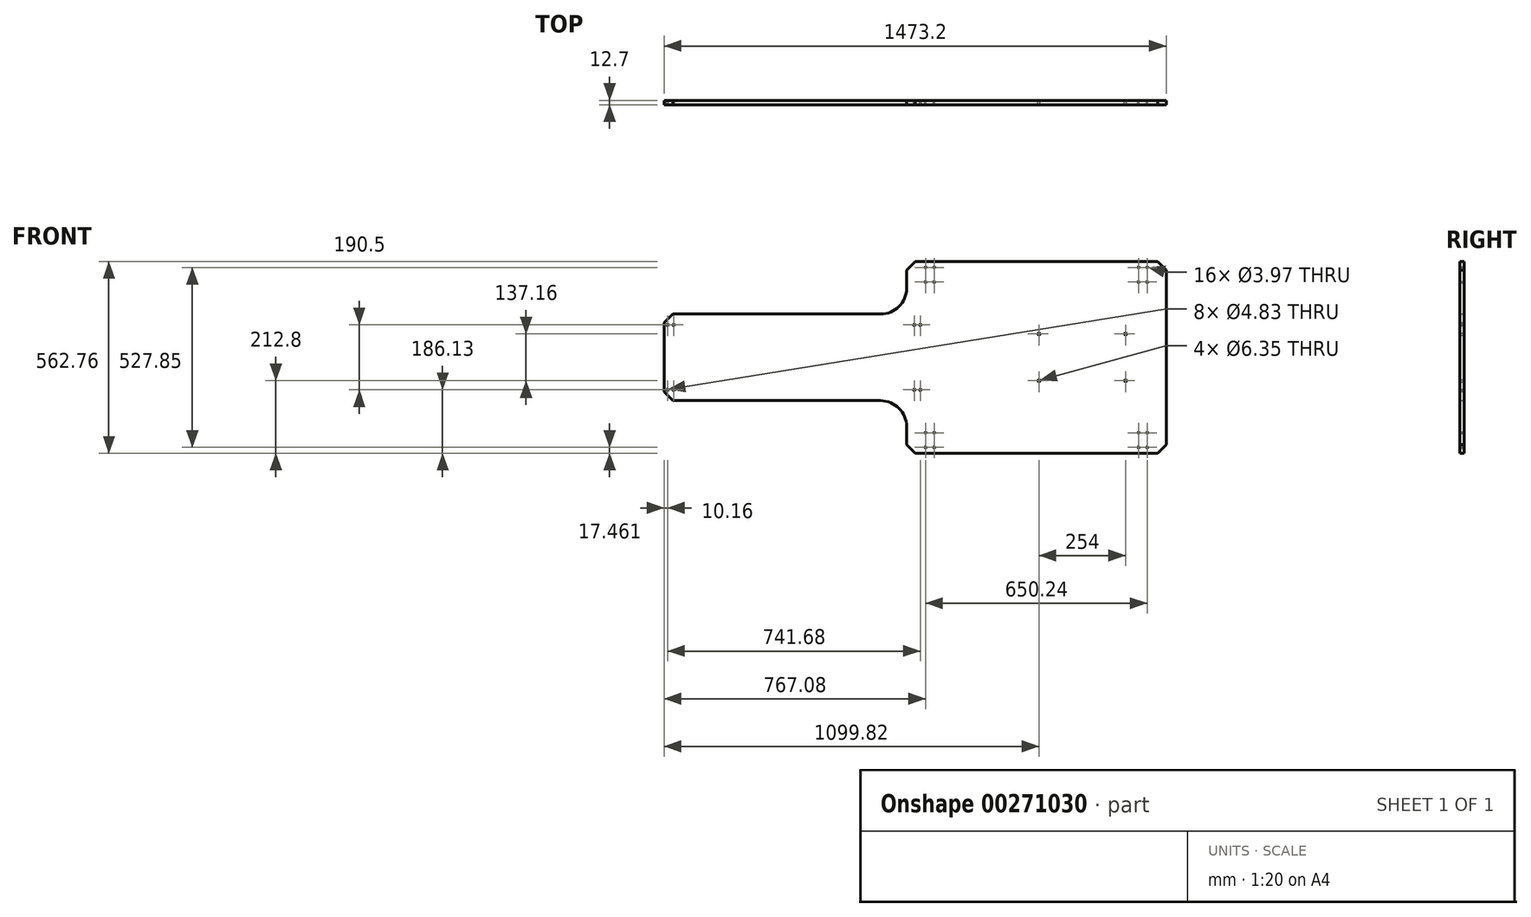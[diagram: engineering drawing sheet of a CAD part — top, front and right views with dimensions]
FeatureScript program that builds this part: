
annotation { "Feature Type Name" : "Feature", "Feature Type Description" : "" }
export const myFeature = defineFeature(function(context is Context, id is Id, definition is map)
    precondition{}
    {
        {
            var Q0;
            Q0=qCreatedBy(makeId("Front.planeOp"),FACE);
            var sketch = newSketch(context, id + "F0", { "sketchPlane" : qUnion([Q0])});
            skLineSegment(sketch, "E0.bottom", {"start": v(0, 0) * mm, "end": v(635, 0) * mm});
            skLineSegment(sketch, "E0.top", {"start": v(0, 254) * mm, "end": v(635, 254) * mm});
            skLineSegment(sketch, "E0.left", {"start": v(0, 0) * mm, "end": v(0, 254) * mm});
            skLineSegment(sketch, "E1.bottom", {"start": v(711.2, -154.38) * mm, "end": v(1473.2, -154.38) * mm});
            skLineSegment(sketch, "E1.top", {"start": v(711.2, 408.38) * mm, "end": v(1473.2, 408.38) * mm});
            skLineSegment(sketch, "E1.left", {"start": v(711.2, -154.38) * mm, "end": v(711.2, -76.2) * mm});
            skLineSegment(sketch, "E1.right", {"start": v(1473.2, -154.38) * mm, "end": v(1473.2, 408.38) * mm});
            skLineSegment(sketch, "E2.trimOffspring", {"start": v(711.2, 330.2) * mm, "end": v(711.2, 408.38) * mm});
            skPoint(sketch, "E3.visualSharp", {"position": v(711.2, 254) * mm});
            skArc(sketch, "E3.filletArc", {"start": v(635, 254) * mm, "mid": v(688.88, 276.32) * mm, "end": v(711.2, 330.2) * mm});
            skPoint(sketch, "E4.visualSharp", {"position": v(711.2, 0) * mm});
            skArc(sketch, "E4.filletArc", {"start": v(711.2, -76.2) * mm, "mid": v(688.88, -22.32) * mm, "end": v(635, 0) * mm});
            skSolve(sketch);
        }
        {
            var Q0;
            Q0 = qSketchRegion(id + "F0", true);
            extrude(context, id + "F1", {"entities" : qUnion([Q0]), "depth" : 12.7 * mm});
        }
        {
            var Q0;
            Q0=makeQuery(id+"F1.opExtrude","SWEPT_EDGE",EDGE,{"disambiguationData":[OSD([sQuery(id+"F0.wireOp",EDGE,"E1.top"),sQuery(id+"F0.wireOp",EDGE,"E2.trimOffspring")])]});
            var Q1;
            Q1=makeQuery(id+"F1.opExtrude","SWEPT_EDGE",EDGE,{"disambiguationData":[OSD([sQuery(id+"F0.wireOp",EDGE,"E1.top"),sQuery(id+"F0.wireOp",EDGE,"E1.right")])]});
            var Q2;
            Q2=makeQuery(id+"F1.opExtrude","SWEPT_EDGE",EDGE,{"disambiguationData":[OSD([sQuery(id+"F0.wireOp",EDGE,"E1.bottom"),sQuery(id+"F0.wireOp",EDGE,"E1.right")])]});
            var Q3;
            Q3=makeQuery(id+"F1.opExtrude","SWEPT_EDGE",EDGE,{"disambiguationData":[OSD([sQuery(id+"F0.wireOp",EDGE,"E1.bottom"),sQuery(id+"F0.wireOp",EDGE,"E1.left")])]});
            var Q4;
            Q4=makeQuery(id+"F1.opExtrude","SWEPT_EDGE",EDGE,{"disambiguationData":[OSD([sQuery(id+"F0.wireOp",EDGE,"E0.bottom"),sQuery(id+"F0.wireOp",EDGE,"E0.left")])]});
            var Q5;
            Q5=makeQuery(id+"F1.opExtrude","SWEPT_EDGE",EDGE,{"disambiguationData":[OSD([sQuery(id+"F0.wireOp",EDGE,"E0.top"),sQuery(id+"F0.wireOp",EDGE,"E0.left")])]});
            chamfer(context, id + "F2", {"entities" : qUnion([Q0, Q1, Q2, Q3, Q4, Q5]), "width" : 25.4 * mm, "tangentPropagation" : true});
        }
        {
            var Q0;
            Q0=makeQuery(id+"F1.opExtrude","CAP_FACE",FACE,{"disambiguationData":[OSD([sQuery(id+"F0.wireOp",EDGE,"E0.bottom"),sQuery(id+"F0.wireOp",EDGE,"E0.top"),sQuery(id+"F0.wireOp",EDGE,"E0.left"),sQuery(id+"F0.wireOp",EDGE,"E1.bottom"),sQuery(id+"F0.wireOp",EDGE,"E1.top"),sQuery(id+"F0.wireOp",EDGE,"E1.left"),sQuery(id+"F0.wireOp",EDGE,"E1.right"),sQuery(id+"F0.wireOp",EDGE,"E2.trimOffspring"),sQuery(id+"F0.wireOp",EDGE,"E3.filletArc"),sQuery(id+"F0.wireOp",EDGE,"E4.filletArc")])],"isStart":false});
            var sketch = newSketch(context, id + "F3", { "sketchPlane" : qUnion([Q0])});
            skPoint(sketch, "E5", {"position": v(1391.92, -94.06) * mm});
            skPoint(sketch, "E6", {"position": v(1417.32, -94.06) * mm});
            skPoint(sketch, "E7", {"position": v(1391.92, -136.92) * mm});
            skPoint(sketch, "E8", {"position": v(1417.32, -136.92) * mm});
            skPoint(sketch, "E9", {"position": v(767.08, -94.06) * mm});
            skPoint(sketch, "E10", {"position": v(792.48, -94.06) * mm});
            skPoint(sketch, "E11", {"position": v(792.48, -136.92) * mm});
            skPoint(sketch, "E12", {"position": v(767.08, -136.92) * mm});
            skPoint(sketch, "E13", {"position": v(767.08, 390.93) * mm});
            skPoint(sketch, "E14", {"position": v(792.48, 390.93) * mm});
            skPoint(sketch, "E15", {"position": v(792.48, 348.06) * mm});
            skPoint(sketch, "E16", {"position": v(767.08, 348.06) * mm});
            skPoint(sketch, "E17", {"position": v(1391.92, 348.06) * mm});
            skPoint(sketch, "E18", {"position": v(1391.92, 390.93) * mm});
            skPoint(sketch, "E19", {"position": v(1417.32, 390.93) * mm});
            skPoint(sketch, "E20", {"position": v(1417.32, 348.06) * mm});
            skSolve(sketch);
        }
        {
            var Q0;
            Q0=sQuery(id+"F3.wireOp",VERTEX,"E13");
            var Q1;
            Q1=sQuery(id+"F3.wireOp",VERTEX,"E16");
            var Q2;
            Q2=sQuery(id+"F3.wireOp",VERTEX,"E15");
            var Q3;
            Q3=sQuery(id+"F3.wireOp",VERTEX,"E14");
            var Q4;
            Q4=sQuery(id+"F3.wireOp",VERTEX,"E9");
            var Q5;
            Q5=sQuery(id+"F3.wireOp",VERTEX,"E12");
            var Q6;
            Q6=sQuery(id+"F3.wireOp",VERTEX,"E11");
            var Q7;
            Q7=sQuery(id+"F3.wireOp",VERTEX,"E10");
            var Q8;
            Q8=sQuery(id+"F3.wireOp",VERTEX,"E5");
            var Q9;
            Q9=sQuery(id+"F3.wireOp",VERTEX,"E7");
            var Q10;
            Q10=sQuery(id+"F3.wireOp",VERTEX,"E8");
            var Q11;
            Q11=sQuery(id+"F3.wireOp",VERTEX,"E6");
            var Q12;
            Q12=sQuery(id+"F3.wireOp",VERTEX,"E17");
            var Q13;
            Q13=sQuery(id+"F3.wireOp",VERTEX,"E18");
            var Q14;
            Q14=sQuery(id+"F3.wireOp",VERTEX,"E19");
            var Q15;
            Q15=sQuery(id+"F3.wireOp",VERTEX,"E20");
            var Q16;
            Q16=makeQuery(id+"F1.opExtrude","SWEPT_BODY",BODY,{"disambiguationData":[OSD([sQuery(id+"F0.wireOp",EDGE,"E0.bottom"),sQuery(id+"F0.wireOp",EDGE,"E0.top"),sQuery(id+"F0.wireOp",EDGE,"E0.left"),sQuery(id+"F0.wireOp",EDGE,"E1.bottom"),sQuery(id+"F0.wireOp",EDGE,"E1.top"),sQuery(id+"F0.wireOp",EDGE,"E1.left"),sQuery(id+"F0.wireOp",EDGE,"E1.right"),sQuery(id+"F0.wireOp",EDGE,"E2.trimOffspring"),sQuery(id+"F0.wireOp",EDGE,"E3.filletArc"),sQuery(id+"F0.wireOp",EDGE,"E4.filletArc")])]});
            hole(context, id + "F4", {"style" : HoleStyle.SIMPLE, "endStyle" : HoleEndStyle.THROUGH, "holeDiameter" : 3.97 * mm, "tappedDepth" : 12.7 * mm, "tapClearance" : 3, "locations" : qUnion([Q0, Q1, Q2, Q3, Q4, Q5, Q6, Q7, Q8, Q9, Q10, Q11, Q12, Q13, Q14, Q15]), "scope" : qUnion([Q16])});
        }
        {
            var Q0;
            Q0=makeQuery(id+"F1.opExtrude","CAP_FACE",FACE,{"disambiguationData":[OSD([sQuery(id+"F0.wireOp",EDGE,"E0.bottom"),sQuery(id+"F0.wireOp",EDGE,"E0.top"),sQuery(id+"F0.wireOp",EDGE,"E0.left"),sQuery(id+"F0.wireOp",EDGE,"E1.bottom"),sQuery(id+"F0.wireOp",EDGE,"E1.top"),sQuery(id+"F0.wireOp",EDGE,"E1.left"),sQuery(id+"F0.wireOp",EDGE,"E1.right"),sQuery(id+"F0.wireOp",EDGE,"E2.trimOffspring"),sQuery(id+"F0.wireOp",EDGE,"E3.filletArc"),sQuery(id+"F0.wireOp",EDGE,"E4.filletArc")])],"isStart":false});
            var sketch = newSketch(context, id + "F5", { "sketchPlane" : qUnion([Q0])});
            skPoint(sketch, "E21", {"position": v(1099.82, 195.58) * mm});
            skPoint(sketch, "E22", {"position": v(1353.82, 195.58) * mm});
            skPoint(sketch, "E23", {"position": v(1353.82, 58.42) * mm});
            skPoint(sketch, "E24", {"position": v(1099.82, 58.42) * mm});
            skSolve(sketch);
        }
        {
            var Q0;
            Q0=sQuery(id+"F5.wireOp",VERTEX,"E21");
            var Q1;
            Q1=sQuery(id+"F5.wireOp",VERTEX,"E24");
            var Q2;
            Q2=sQuery(id+"F5.wireOp",VERTEX,"E23");
            var Q3;
            Q3=sQuery(id+"F5.wireOp",VERTEX,"E22");
            var Q4;
            Q4=makeQuery(id+"F1.opExtrude","SWEPT_BODY",BODY,{"disambiguationData":[OSD([sQuery(id+"F0.wireOp",EDGE,"E0.bottom"),sQuery(id+"F0.wireOp",EDGE,"E0.top"),sQuery(id+"F0.wireOp",EDGE,"E0.left"),sQuery(id+"F0.wireOp",EDGE,"E1.bottom"),sQuery(id+"F0.wireOp",EDGE,"E1.top"),sQuery(id+"F0.wireOp",EDGE,"E1.left"),sQuery(id+"F0.wireOp",EDGE,"E1.right"),sQuery(id+"F0.wireOp",EDGE,"E2.trimOffspring"),sQuery(id+"F0.wireOp",EDGE,"E3.filletArc"),sQuery(id+"F0.wireOp",EDGE,"E4.filletArc")])]});
            hole(context, id + "F6", {"style" : HoleStyle.SIMPLE, "endStyle" : HoleEndStyle.THROUGH, "holeDiameter" : 6.35 * mm, "tappedDepth" : 12.7 * mm, "tapClearance" : 3, "locations" : qUnion([Q0, Q1, Q2, Q3]), "scope" : qUnion([Q4])});
        }
        {
            var Q0;
            Q0=makeQuery(id+"F1.opExtrude","CAP_FACE",FACE,{"disambiguationData":[OSD([sQuery(id+"F0.wireOp",EDGE,"E0.bottom"),sQuery(id+"F0.wireOp",EDGE,"E0.top"),sQuery(id+"F0.wireOp",EDGE,"E0.left"),sQuery(id+"F0.wireOp",EDGE,"E1.bottom"),sQuery(id+"F0.wireOp",EDGE,"E1.top"),sQuery(id+"F0.wireOp",EDGE,"E1.left"),sQuery(id+"F0.wireOp",EDGE,"E1.right"),sQuery(id+"F0.wireOp",EDGE,"E2.trimOffspring"),sQuery(id+"F0.wireOp",EDGE,"E3.filletArc"),sQuery(id+"F0.wireOp",EDGE,"E4.filletArc")])],"isStart":false});
            var sketch = newSketch(context, id + "F7", { "sketchPlane" : qUnion([Q0])});
            skPoint(sketch, "E25", {"position": v(10.16, 222.25) * mm});
            skPoint(sketch, "E26", {"position": v(27.94, 222.25) * mm});
            skPoint(sketch, "E27", {"position": v(734.06, 222.25) * mm});
            skPoint(sketch, "E28", {"position": v(751.84, 222.25) * mm});
            skPoint(sketch, "E29", {"position": v(10.16, 31.75) * mm});
            skPoint(sketch, "E30", {"position": v(27.94, 31.75) * mm});
            skPoint(sketch, "E31", {"position": v(734.06, 31.75) * mm});
            skPoint(sketch, "E32", {"position": v(751.84, 31.75) * mm});
            skSolve(sketch);
        }
        {
            var Q0;
            Q0=sQuery(id+"F7.wireOp",VERTEX,"E25");
            var Q1;
            Q1=sQuery(id+"F7.wireOp",VERTEX,"E26");
            var Q2;
            Q2=sQuery(id+"F7.wireOp",VERTEX,"E29");
            var Q3;
            Q3=sQuery(id+"F7.wireOp",VERTEX,"E30");
            var Q4;
            Q4=sQuery(id+"F7.wireOp",VERTEX,"E31");
            var Q5;
            Q5=sQuery(id+"F7.wireOp",VERTEX,"E28");
            var Q6;
            Q6=sQuery(id+"F7.wireOp",VERTEX,"E27");
            var Q7;
            Q7=sQuery(id+"F7.wireOp",VERTEX,"E32");
            var Q8;
            Q8=makeQuery(id+"F1.opExtrude","SWEPT_BODY",BODY,{"disambiguationData":[OSD([sQuery(id+"F0.wireOp",EDGE,"E0.bottom"),sQuery(id+"F0.wireOp",EDGE,"E0.top"),sQuery(id+"F0.wireOp",EDGE,"E0.left"),sQuery(id+"F0.wireOp",EDGE,"E1.bottom"),sQuery(id+"F0.wireOp",EDGE,"E1.top"),sQuery(id+"F0.wireOp",EDGE,"E1.left"),sQuery(id+"F0.wireOp",EDGE,"E1.right"),sQuery(id+"F0.wireOp",EDGE,"E2.trimOffspring"),sQuery(id+"F0.wireOp",EDGE,"E3.filletArc"),sQuery(id+"F0.wireOp",EDGE,"E4.filletArc")])]});
            hole(context, id + "F8", {"style" : HoleStyle.SIMPLE, "endStyle" : HoleEndStyle.THROUGH, "holeDiameter" : 4.83 * mm, "tappedDepth" : 12.7 * mm, "tapClearance" : 3, "locations" : qUnion([Q0, Q1, Q2, Q3, Q4, Q5, Q6, Q7]), "scope" : qUnion([Q8])});
        }
    });
